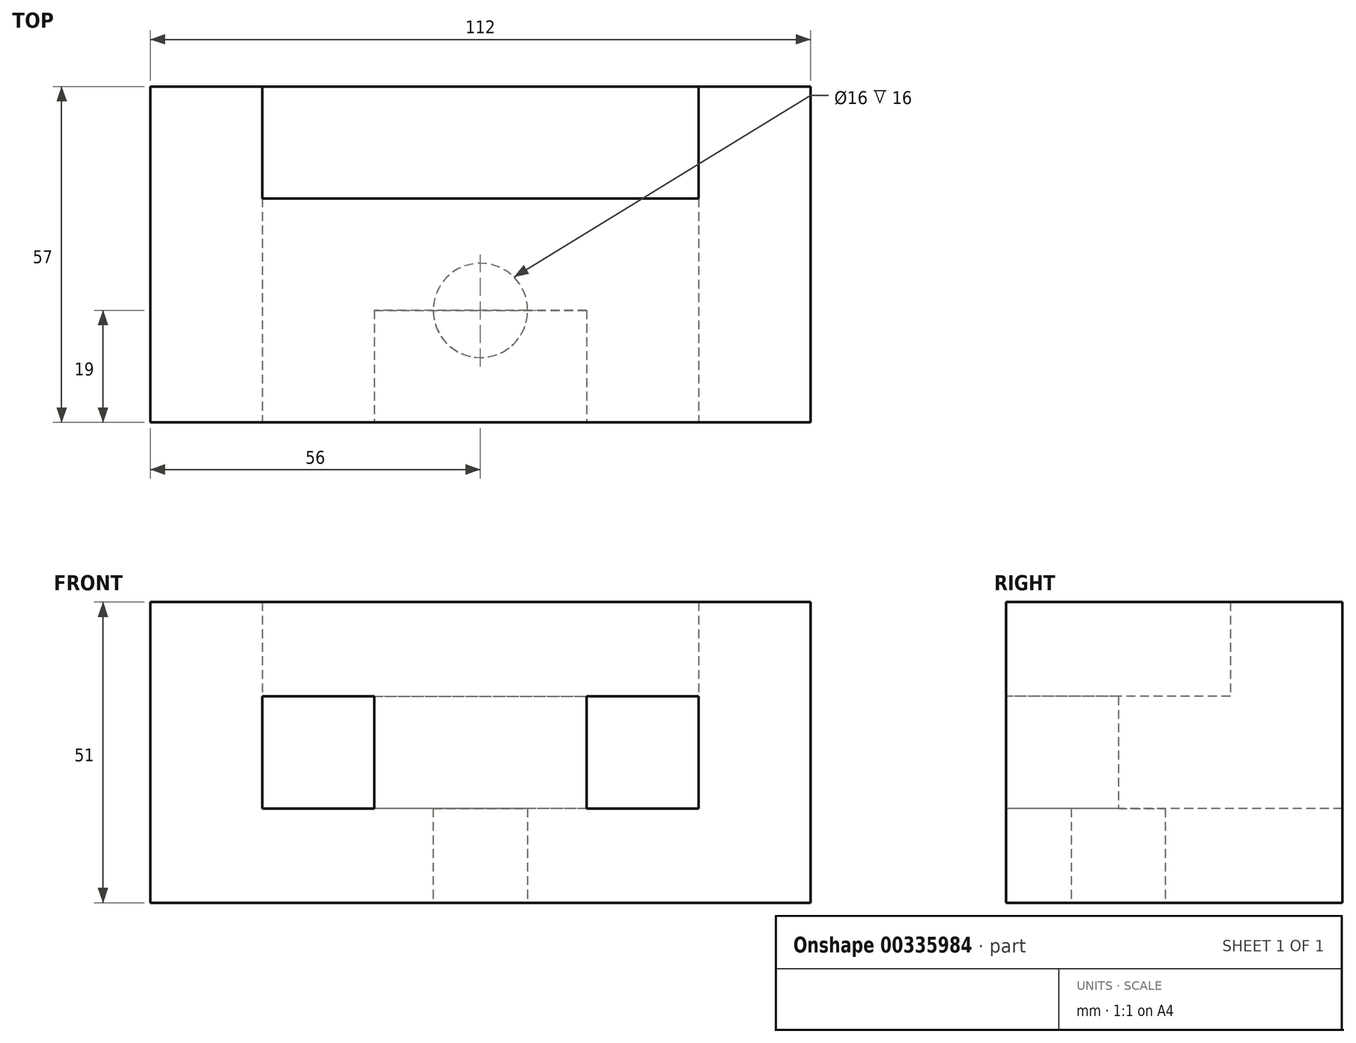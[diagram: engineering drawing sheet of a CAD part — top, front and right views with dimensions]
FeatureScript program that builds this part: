
annotation { "Feature Type Name" : "Feature", "Feature Type Description" : "" }
export const myFeature = defineFeature(function(context is Context, id is Id, definition is map)
    precondition{}
    {
        {
            var Q0;
            Q0=qCreatedBy(makeId("Front.planeOp"),FACE);
            var sketch = newSketch(context, id + "F0", { "sketchPlane" : qUnion([Q0])});
            skLineSegment(sketch, "E0", {"start": v(0, 0) * mm, "end": v(0, 51) * mm});
            skLineSegment(sketch, "E1", {"start": v(0, 51) * mm, "end": v(19, 51) * mm});
            skLineSegment(sketch, "E2", {"start": v(0, 0) * mm, "end": v(112, 0) * mm});
            skLineSegment(sketch, "E3", {"start": v(112, 0) * mm, "end": v(112, 51) * mm});
            skLineSegment(sketch, "E4", {"start": v(112, 51) * mm, "end": v(93, 51) * mm});
            skLineSegment(sketch, "E5", {"start": v(93, 51) * mm, "end": v(93, 16) * mm});
            skLineSegment(sketch, "E6", {"start": v(93, 16) * mm, "end": v(19, 16) * mm});
            skLineSegment(sketch, "E7", {"start": v(19, 51) * mm, "end": v(93, 51) * mm});
            skLineSegment(sketch, "E8", {"start": v(19, 51) * mm, "end": v(19, 35) * mm});
            skLineSegment(sketch, "E9", {"start": v(19, 35) * mm, "end": v(19, 16) * mm});
            skLineSegment(sketch, "E10", {"start": v(19, 35) * mm, "end": v(93, 35) * mm});
            skLineSegment(sketch, "E11", {"start": v(19, 35) * mm, "end": v(38, 35) * mm, "construction": true});
            skLineSegment(sketch, "E12", {"start": v(38, 35) * mm, "end": v(38, 16) * mm});
            skLineSegment(sketch, "E13", {"start": v(93, 35) * mm, "end": v(74, 35) * mm, "construction": true});
            skLineSegment(sketch, "E14", {"start": v(74, 35) * mm, "end": v(74, 16) * mm});
            skSolve(sketch);
        }
        {
            var Q0;
            {var subQ3=sQuery(id+"F0.wireOp",EDGE,"E7");Q0=makeQuery(id+"F0.imprint","IMPRINT",FACE,{"disambiguationData":[TD([[makeQuery(id+"F0.imprint","IMPRINT",EDGE,{"derivedFrom":subQ3}),-1.0]])]});}
            extrude(context, id + "F1", {"entities" : qUnion([Q0]), "oppositeDirection" : true, "depth" : 38 * mm});
        }
        {
            var Q0;
            {var subQ0=sQuery(id+"F0.wireOp",EDGE,"E12");Q0=makeQuery(id+"F0.imprint","IMPRINT",FACE,{"disambiguationData":[TD([[makeQuery(id+"F0.imprint","IMPRINT",EDGE,{"derivedFrom":subQ0}),1.0]])]});}
            extrude(context, id + "F2", {"entities" : qUnion([Q0]), "operationType" : NewBodyOperationType.ADD, "oppositeDirection" : true, "depth" : 19 * mm});
        }
        {
            var Q0;
            Q0=makeQuery(id+"F0.imprint","IMPRINT",FACE,{"disambiguationData":[TD([[makeQuery(id+"F0.imprint","IMPRINT",EDGE,{"derivedFrom":sQuery(id+"F0.wireOp",EDGE,"E0")}),-1.0]])]});
            extrude(context, id + "F3", {"entities" : qUnion([Q0]), "operationType" : NewBodyOperationType.ADD, "oppositeDirection" : true, "depth" : 57 * mm});
        }
        {
            var Q0;
            Q0=makeQuery(id+"F3.opExtrude","SWEPT_FACE",FACE,{"disambiguationData":[OSD([sQuery(id+"F0.wireOp",EDGE,"E2")])]});
            var sketch = newSketch(context, id + "F4", { "sketchPlane" : qUnion([Q0])});
            skLineSegment(sketch, "E15", {"start": v(0, 0) * mm, "end": v(56, 0) * mm, "construction": true});
            skLineSegment(sketch, "E16", {"start": v(56, 0) * mm, "end": v(56, -19) * mm, "construction": true});
            skCircle(sketch, "E17", {"center": v(56, -19) * mm, "radius": 8 * mm});
            skSolve(sketch);
        }
        {
            var Q0;
            Q0=makeQuery(id+"F4.imprint","IMPRINT",FACE,{"disambiguationData":[TD([[makeQuery(id+"F4.imprint","IMPRINT",EDGE,{"derivedFrom":sQuery(id+"F4.wireOp",EDGE,"E17")}),1.0]])]});
            extrude(context, id + "F5", {"entities" : qUnion([Q0]), "operationType" : NewBodyOperationType.REMOVE, "oppositeDirection" : true, "depth" : 16 * mm});
        }
    });
